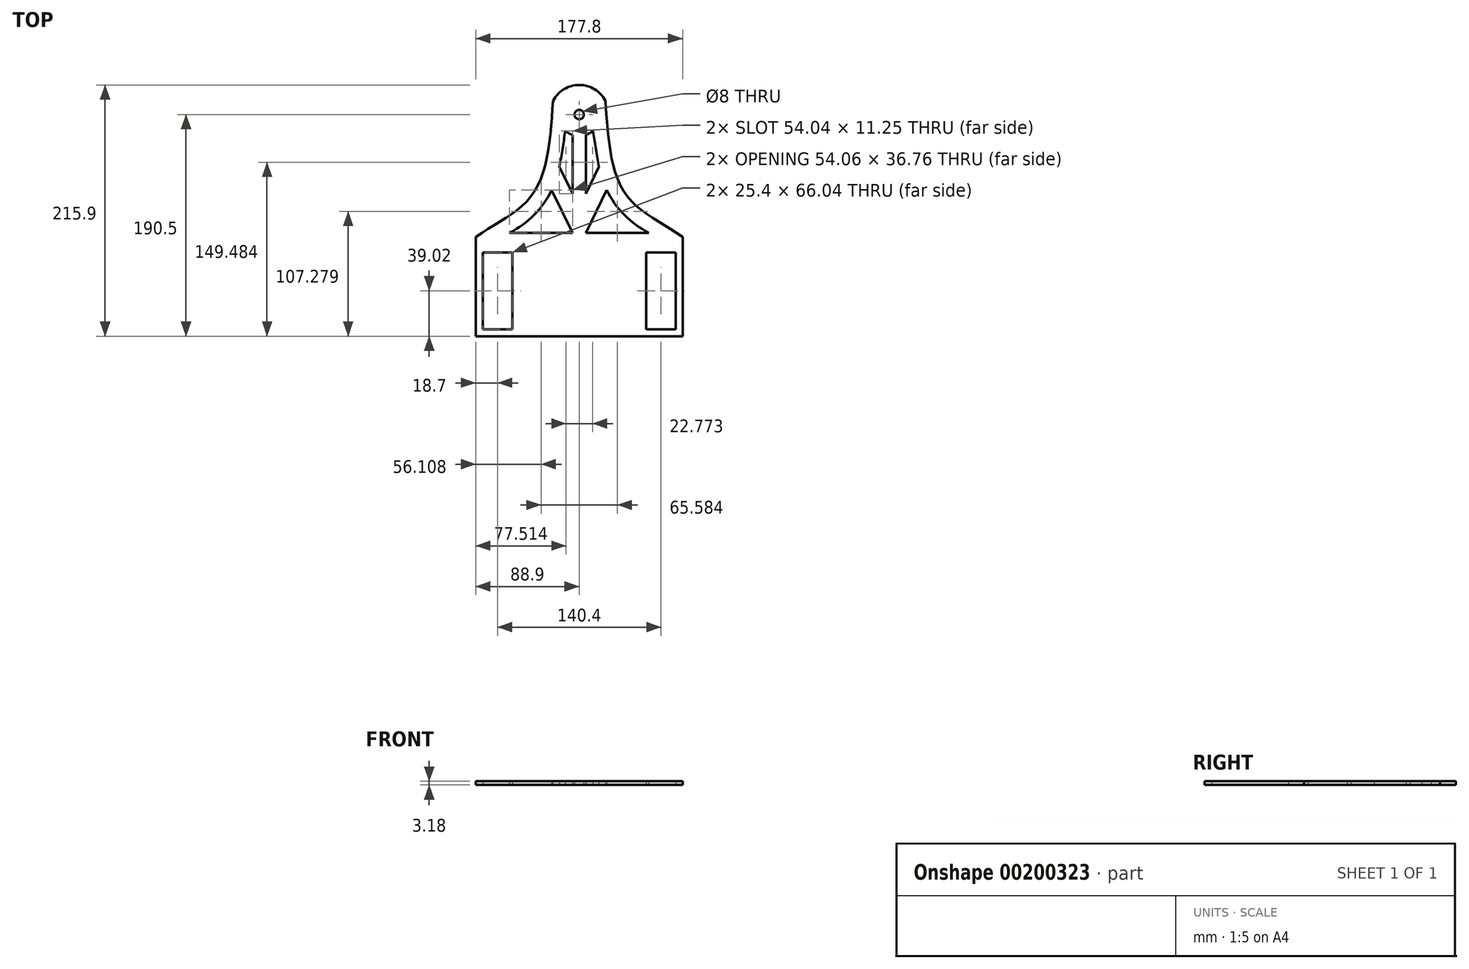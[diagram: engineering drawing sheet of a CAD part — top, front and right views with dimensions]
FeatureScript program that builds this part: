
annotation { "Feature Type Name" : "Feature", "Feature Type Description" : "" }
export const myFeature = defineFeature(function(context is Context, id is Id, definition is map)
    precondition{}
    {
        {
            var Q0;
            Q0=qCreatedBy(makeId("Top.planeOp"),FACE);
            var sketch = newSketch(context, id + "F0", { "sketchPlane" : qUnion([Q0])});
            skPoint(sketch, "E0.middle", {"position": v(0, 0) * mm});
            skPoint(sketch, "E1.orphan", {"position": v(-101.6, 127) * mm});
            skPoint(sketch, "E2.orphan", {"position": v(101.6, 127) * mm});
            skLineSegment(sketch, "E3", {"start": v(0, 127) * mm, "end": v(0, 101.6) * mm, "construction": true});
            skArc(sketch, "E4", {"start": v(22.52, 113.35) * mm, "mid": v(0, 127) * mm, "end": v(-22.52, 113.35) * mm});
            skCircle(sketch, "E5", {"center": v(0, 101.6) * mm, "radius": 107.95 * mm, "construction": true});
            skCircle(sketch, "E6", {"center": v(0, 101.6) * mm, "radius": 4 * mm});
            skLineSegment(sketch, "E7", {"start": v(0, 0) * mm, "end": v(0, -88.9) * mm, "construction": true});
            skLineSegment(sketch, "E8.bottom", {"start": v(-88.9, -88.9) * mm, "end": v(88.9, -88.9) * mm});
            skPoint(sketch, "E8.middle", {"position": v(0, -44.45) * mm});
            skLineSegment(sketch, "E9.bottom", {"start": v(-57.5, -82.9) * mm, "end": v(-82.9, -82.9) * mm});
            skLineSegment(sketch, "E9.top", {"start": v(-57.5, -16.86) * mm, "end": v(-82.9, -16.86) * mm});
            skLineSegment(sketch, "E9.left", {"start": v(-57.5, -82.9) * mm, "end": v(-57.5, -16.86) * mm});
            skLineSegment(sketch, "E9.right", {"start": v(-82.9, -82.9) * mm, "end": v(-82.9, -16.86) * mm});
            skPoint(sketch, "E9.middle", {"position": v(-70.2, -49.88) * mm});
            skLineSegment(sketch, "E10.MirrorCS", {"start": v(57.5, -82.9) * mm, "end": v(57.5, -16.86) * mm});
            skLineSegment(sketch, "E11.MirrorCS", {"start": v(57.5, -16.86) * mm, "end": v(82.9, -16.86) * mm});
            skLineSegment(sketch, "E12.MirrorCS", {"start": v(82.9, -82.9) * mm, "end": v(82.9, -16.86) * mm});
            skLineSegment(sketch, "E13.MirrorCS", {"start": v(57.5, -82.9) * mm, "end": v(82.9, -82.9) * mm});
            skPoint(sketch, "E14.orphan", {"position": v(-88.9, 0) * mm});
            skPoint(sketch, "E15.orphan", {"position": v(88.9, 0) * mm});
            skLineSegment(sketch, "E16", {"start": v(-88.9, -3.66) * mm, "end": v(88.9, -3.66) * mm});
            skLineSegment(sketch, "E17", {"start": v(-88.9, -3.66) * mm, "end": v(-88.9, -88.9) * mm});
            skLineSegment(sketch, "E18", {"start": v(88.9, -3.66) * mm, "end": v(88.9, -88.9) * mm});
            skFitSpline(sketch, "E19", {"points": [v(-22.52, 113.35) * mm, v(-38.75, 34.9) * mm, v(-88.9, -3.66) * mm], "startDerivative": vector(-12.23, -164.97) * mm, "endDerivative": vector(-121.97, -84.06) * mm});
            skFitSpline(sketch, "E20.MirrorCS", {"points": [v(22.52, 113.35) * mm, v(38.75, 34.9) * mm, v(88.9, -3.66) * mm], "startDerivative": vector(12.23, -164.97) * mm, "endDerivative": vector(121.97, -84.06) * mm});
            skArc(sketch, "E21", {"start": v(5.76, 84.13) * mm, "mid": v(9.02, 85.56) * mm, "end": v(11.95, 87.6) * mm});
            skLineSegment(sketch, "E22", {"start": v(-23.65, 36.76) * mm, "end": v(-5.76, 0) * mm});
            skLineSegment(sketch, "E23", {"start": v(-17.01, 56.68) * mm, "end": v(-5.76, 33.56) * mm});
            skLineSegment(sketch, "E24", {"start": v(-5.76, 33.56) * mm, "end": v(-5.76, 84.13) * mm});
            skLineSegment(sketch, "E25.MirrorCS", {"start": v(17.01, 56.68) * mm, "end": v(5.76, 33.56) * mm});
            skLineSegment(sketch, "E26.MirrorCS", {"start": v(5.76, 33.56) * mm, "end": v(5.76, 84.13) * mm});
            skLineSegment(sketch, "E27.MirrorCS", {"start": v(23.65, 36.76) * mm, "end": v(5.76, 0) * mm});
            skLineSegment(sketch, "E28", {"start": v(-11.95, 87.6) * mm, "end": v(11.95, 87.6) * mm, "construction": true});
            skArc(sketch, "E29", {"start": v(-17.01, 56.68) * mm, "mid": v(-14.35, 72.12) * mm, "end": v(-11.95, 87.6) * mm});
            skArc(sketch, "E30.MirrorCS", {"start": v(17.01, 56.68) * mm, "mid": v(14.35, 72.12) * mm, "end": v(11.95, 87.6) * mm});
            skArc(sketch, "E31.trimOffspring", {"start": v(-11.95, 87.6) * mm, "mid": v(-9.02, 85.56) * mm, "end": v(-5.76, 84.13) * mm});
            skLineSegment(sketch, "E32", {"start": v(-5.76, 0) * mm, "end": v(-59.82, 0) * mm});
            skArc(sketch, "E33", {"start": v(-59.82, 0) * mm, "mid": v(-38.71, 15.4) * mm, "end": v(-23.65, 36.76) * mm});
            skArc(sketch, "E34.MirrorCS", {"start": v(59.82, 0) * mm, "mid": v(38.71, 15.4) * mm, "end": v(23.65, 36.76) * mm});
            skLineSegment(sketch, "E35.MirrorCS", {"start": v(5.76, 0) * mm, "end": v(59.82, 0) * mm});
            skSolve(sketch);
        }
        {
            var Q0;
            Q0=makeQuery(id+"F0.imprint","IMPRINT",FACE,{"disambiguationData":[TD([[makeQuery(id+"F0.imprint","IMPRINT",EDGE,{"derivedFrom":sQuery(id+"F0.wireOp",EDGE,"E4")}),1.0]])]});
            var Q1;
            Q1=makeQuery(id+"F0.imprint","IMPRINT",FACE,{"disambiguationData":[TD([[makeQuery(id+"F0.imprint","IMPRINT",EDGE,{"derivedFrom":sQuery(id+"F0.wireOp",EDGE,"E8.bottom")}),1.0]])]});
            extrude(context, id + "F1", {"entities" : qUnion([Q0, Q1]), "depth" : 3.17 * mm});
        }
    });
